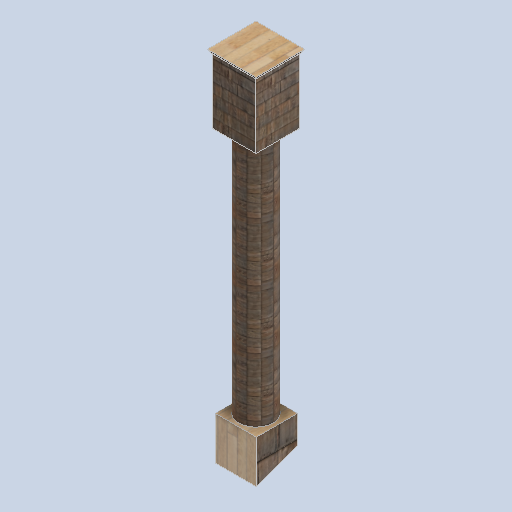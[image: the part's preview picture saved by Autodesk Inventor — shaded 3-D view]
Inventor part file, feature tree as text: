
AUTODESK INVENTOR PART (.ipt)
format: ipt  version: 2024.2 (Build 282272000, 272)  size: 173,568 bytes
history: native  units: in
note: dims shown in document units (in); Inventor stores cm internally (conversion verified against a paired STEP export)
features: sketch x5, other x3, plane x1
ambient origin geometry x8: Origin, YZ Plane, XZ Plane, XY Plane, X Axis, Y Axis, Z Axis, Center Point
bodies: Solid1 (feature_tree)
feature tree (9):
  other  "side_pillar_01.ipt"
  other  "Solid1::side_pillar_01.ipt"
  other  "TaggingFeature1"
  sketch  "Sketch1"  dims[d0=0.3937in]
  sketch  "Sketch2"
  sketch  "Sketch3"
  sketch  "Sketch4"
  sketch  "Sketch5"
  plane  "Work Plane3"
